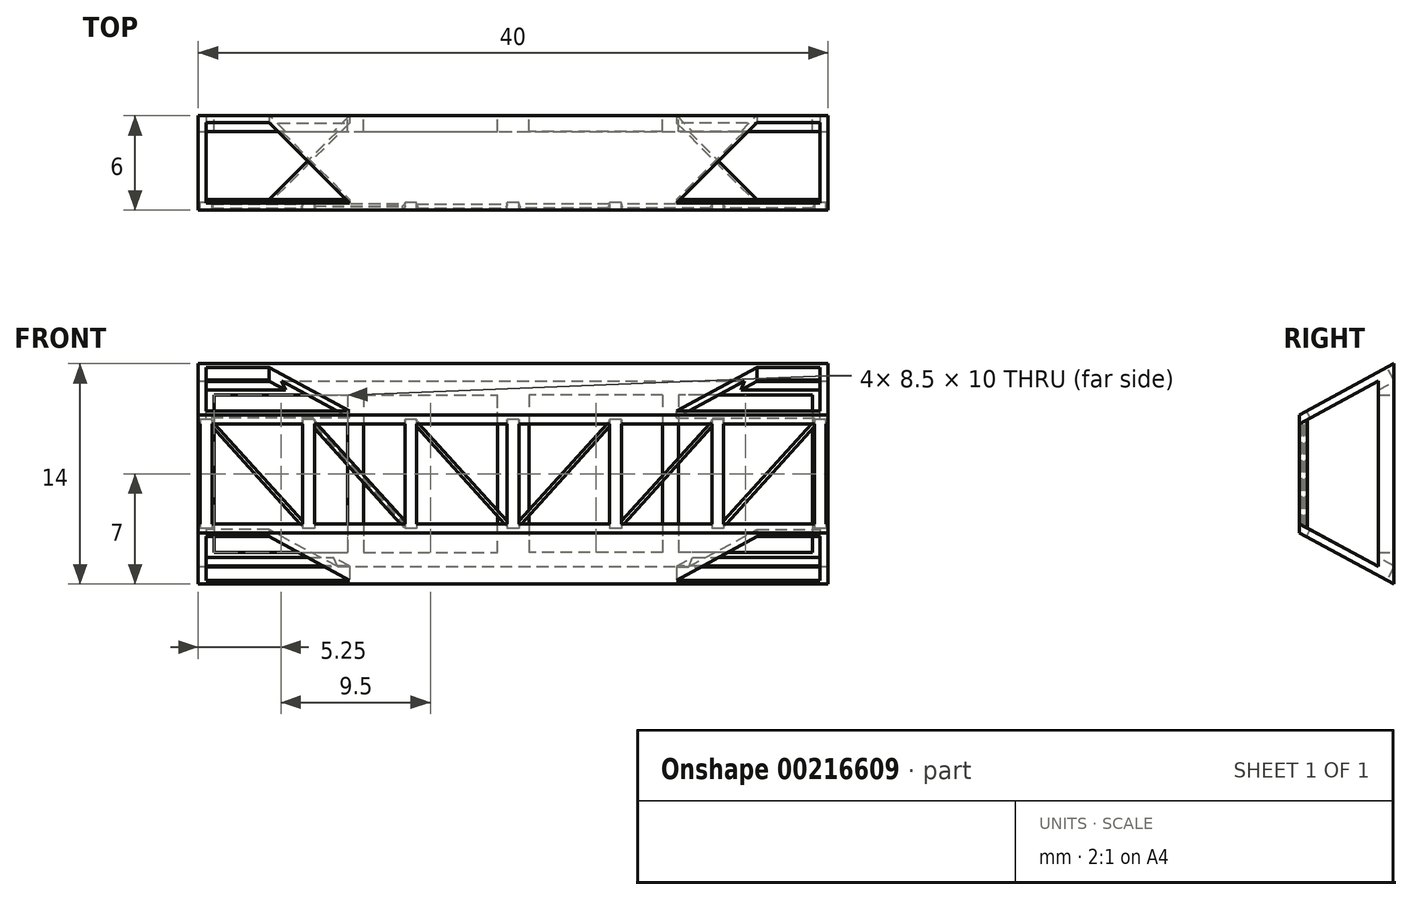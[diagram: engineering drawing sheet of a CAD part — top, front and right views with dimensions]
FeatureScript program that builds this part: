
annotation { "Feature Type Name" : "Feature", "Feature Type Description" : "" }
export const myFeature = defineFeature(function(context is Context, id is Id, definition is map)
    precondition{}
    {
        {
            var Q0;
            Q0=qCreatedBy(makeId("Right.planeOp"),FACE);
            var sketch = newSketch(context, id + "F0", { "sketchPlane" : qUnion([Q0])});
            skLineSegment(sketch, "E0", {"start": v(0, 0) * mm, "end": v(0, 7) * mm});
            skLineSegment(sketch, "E1", {"start": v(0, 0) * mm, "end": v(0, -7) * mm});
            skLineSegment(sketch, "E2", {"start": v(0, 0) * mm, "end": v(-6, 0) * mm});
            skLineSegment(sketch, "E3", {"start": v(-6, 0) * mm, "end": v(-6, 3.75) * mm});
            skLineSegment(sketch, "E4", {"start": v(-6, 3.75) * mm, "end": v(0, 7) * mm});
            skLineSegment(sketch, "E5.MirrorCS", {"start": v(-6, 0) * mm, "end": v(-6, -3.75) * mm});
            skLineSegment(sketch, "E6", {"start": v(-6, -3.75) * mm, "end": v(0, -7) * mm});
            skSolve(sketch);
        }
        {
            var Q0;
            Q0=makeQuery(id+"F0.imprint","IMPRINT",FACE,{"disambiguationData":[TD([[makeQuery(id+"F0.imprint","IMPRINT",EDGE,{"derivedFrom":sQuery(id+"F0.wireOp",EDGE,"E2")}),1.0]])]});
            var Q1;
            Q1=makeQuery(id+"F0.imprint","IMPRINT",FACE,{"disambiguationData":[TD([[makeQuery(id+"F0.imprint","IMPRINT",EDGE,{"derivedFrom":sQuery(id+"F0.wireOp",EDGE,"E0")}),1.0]])]});
            var Q2;
            Q2=sQuery(id+"F0.wireOp",EDGE,"E4");
            var Q3;
            Q3=sQuery(id+"F0.wireOp",EDGE,"E0");
            var Q4;
            Q4=sQuery(id+"F0.wireOp",EDGE,"E3");
            var Q5;
            Q5=sQuery(id+"F0.wireOp",EDGE,"E5.MirrorCS");
            var Q6;
            Q6=sQuery(id+"F0.wireOp",EDGE,"E1");
            var Q7;
            Q7=sQuery(id+"F0.wireOp",EDGE,"E6");
            extrude(context, id + "F1", {"entities" : qUnion([Q0, Q1]), "surfaceEntities" : qUnion([Q2, Q3, Q4, Q5, Q6, Q7]), "depth" : 20 * mm, "hasSecondDirection" : true, "secondDirectionOppositeDirection" : true, "secondDirectionDepth" : 20 * mm});
        }
        {
            var Q0;
            Q0=qCreatedBy(makeId("Right.planeOp"),FACE);
            var sketch = newSketch(context, id + "F2", { "sketchPlane" : qUnion([Q0])});
            skLineSegment(sketch, "E7", {"start": v(-2.76, 4.94) * mm, "end": v(-1, 5.9) * mm});
            skLineSegment(sketch, "E8", {"start": v(-2.76, 4.94) * mm, "end": v(-6, 3.19) * mm});
            skLineSegment(sketch, "E9", {"start": v(-1, 0) * mm, "end": v(-1, -5.89) * mm});
            skLineSegment(sketch, "E10", {"start": v(-1, 5.9) * mm, "end": v(-1, 0) * mm});
            skLineSegment(sketch, "E11", {"start": v(-6, -3.19) * mm, "end": v(-1, -5.89) * mm});
            skLineSegment(sketch, "E12", {"start": v(-6, 3.19) * mm, "end": v(-6, -3.19) * mm});
            skSolve(sketch);
        }
        {
            var Q0;
            Q0=makeQuery(id+"F2.imprint","IMPRINT",FACE,{"disambiguationData":[TD([[makeQuery(id+"F2.imprint","IMPRINT",EDGE,{"derivedFrom":sQuery(id+"F2.wireOp",EDGE,"E7")}),-1.0]])]});
            extrude(context, id + "F3", {"entities" : qUnion([Q0]), "operationType" : NewBodyOperationType.REMOVE, "oppositeDirection" : true, "depth" : 24 * mm, "hasSecondDirection" : true, "secondDirectionOppositeDirection" : false, "secondDirectionDepth" : 24 * mm});
        }
        {
            var Q0;
            Q0=makeQuery(id+"F1.opExtrude","SWEPT_FACE",FACE,{"disambiguationData":[OSD([sQuery(id+"F0.wireOp",EDGE,"E3"),sQuery(id+"F0.wireOp",EDGE,"E5.MirrorCS")])]});
            var sketch = newSketch(context, id + "F4", { "sketchPlane" : qUnion([Q0])});
            skLineSegment(sketch, "E13", {"start": v(0, 0) * mm, "end": v(0, 9.2) * mm, "construction": true});
            skPoint(sketch, "E13.endSnap0", {"position": v(0, 3.75) * mm});
            skLineSegment(sketch, "E14.bottom", {"start": v(0, 3.75) * mm, "end": v(-0.38, 3.75) * mm});
            skLineSegment(sketch, "E14.top", {"start": v(0, -3.75) * mm, "end": v(-0.37, -3.75) * mm});
            skLineSegment(sketch, "E14.left", {"start": v(0, 3.75) * mm, "end": v(0, -3.75) * mm});
            skLineSegment(sketch, "E14.right", {"start": v(-0.38, 3.75) * mm, "end": v(-0.37, -3.75) * mm});
            skLineSegment(sketch, "E15.bottom", {"start": v(0, 3.75) * mm, "end": v(0.38, 3.75) * mm});
            skLineSegment(sketch, "E15.top", {"start": v(0, -3.75) * mm, "end": v(0.38, -3.75) * mm});
            skLineSegment(sketch, "E15.right", {"start": v(0.38, 3.75) * mm, "end": v(0.38, -3.75) * mm});
            skLineSegment(sketch, "E16.trimOffspring", {"start": v(0, 0) * mm, "end": v(0, -10.66) * mm, "construction": true});
            skLineSegment(sketch, "E17.1.0.0", {"start": v(6.5, 3.75) * mm, "end": v(6.5, -3.75) * mm});
            skLineSegment(sketch, "E17.1.0.1", {"start": v(6.88, 3.75) * mm, "end": v(6.88, -3.75) * mm});
            skLineSegment(sketch, "E17.1.0.2", {"start": v(6.13, 3.75) * mm, "end": v(6.13, -3.75) * mm});
            skPoint(sketch, "E17.1.0.3", {"position": v(6.5, 3.75) * mm});
            skLineSegment(sketch, "E17.1.0.4", {"start": v(6.5, 3.75) * mm, "end": v(6.5, -3.75) * mm});
            skLineSegment(sketch, "E17.1.0.5", {"start": v(6.5, -3.75) * mm, "end": v(6.88, -3.75) * mm});
            skLineSegment(sketch, "E17.1.0.6", {"start": v(6.5, 3.75) * mm, "end": v(6.12, 3.75) * mm});
            skLineSegment(sketch, "E17.1.0.7", {"start": v(6.5, -3.75) * mm, "end": v(6.13, -3.75) * mm});
            skLineSegment(sketch, "E17.1.0.8", {"start": v(6.5, 3.75) * mm, "end": v(6.88, 3.75) * mm});
            skLineSegment(sketch, "E17.2.0.0", {"start": v(13, 3.75) * mm, "end": v(13, -3.75) * mm});
            skLineSegment(sketch, "E17.2.0.1", {"start": v(13.38, 3.75) * mm, "end": v(13.38, -3.75) * mm});
            skLineSegment(sketch, "E17.2.0.2", {"start": v(12.62, 3.75) * mm, "end": v(12.63, -3.75) * mm});
            skPoint(sketch, "E17.2.0.3", {"position": v(13, 3.75) * mm});
            skLineSegment(sketch, "E17.2.0.4", {"start": v(13, 3.75) * mm, "end": v(13, -3.75) * mm});
            skLineSegment(sketch, "E17.2.0.5", {"start": v(13, -3.75) * mm, "end": v(13.38, -3.75) * mm});
            skLineSegment(sketch, "E17.2.0.6", {"start": v(13, 3.75) * mm, "end": v(12.62, 3.75) * mm});
            skLineSegment(sketch, "E17.2.0.7", {"start": v(13, -3.75) * mm, "end": v(12.63, -3.75) * mm});
            skLineSegment(sketch, "E17.2.0.8", {"start": v(13, 3.75) * mm, "end": v(13.38, 3.75) * mm});
            skLineSegment(sketch, "E17.3.0.0", {"start": v(19.5, 3.75) * mm, "end": v(19.5, -3.75) * mm});
            skLineSegment(sketch, "E17.3.0.1", {"start": v(19.88, 3.75) * mm, "end": v(19.88, -3.75) * mm});
            skLineSegment(sketch, "E17.3.0.2", {"start": v(19.13, 3.75) * mm, "end": v(19.13, -3.75) * mm});
            skPoint(sketch, "E17.3.0.3", {"position": v(19.5, 3.75) * mm});
            skLineSegment(sketch, "E17.3.0.4", {"start": v(19.5, 3.75) * mm, "end": v(19.5, -3.75) * mm});
            skLineSegment(sketch, "E17.3.0.5", {"start": v(19.5, -3.75) * mm, "end": v(19.88, -3.75) * mm});
            skLineSegment(sketch, "E17.3.0.6", {"start": v(19.5, 3.75) * mm, "end": v(19.13, 3.75) * mm});
            skLineSegment(sketch, "E17.3.0.7", {"start": v(19.5, -3.75) * mm, "end": v(19.13, -3.75) * mm});
            skLineSegment(sketch, "E17.3.0.8", {"start": v(19.5, 3.75) * mm, "end": v(19.88, 3.75) * mm});
            skLineSegment(sketch, "E17.direction1", {"start": v(-0.37, -3.75) * mm, "end": v(6.13, -3.75) * mm, "construction": true});
            skLineSegment(sketch, "E18.1.0.0", {"start": v(-6.88, 3.75) * mm, "end": v(-6.87, -3.75) * mm});
            skLineSegment(sketch, "E18.1.0.1", {"start": v(-6.5, 3.75) * mm, "end": v(-6.5, -3.75) * mm});
            skLineSegment(sketch, "E18.1.0.2", {"start": v(-6.12, 3.75) * mm, "end": v(-6.12, -3.75) * mm});
            skPoint(sketch, "E18.1.0.3", {"position": v(-6.5, 3.75) * mm});
            skLineSegment(sketch, "E18.1.0.4", {"start": v(-6.5, 3.75) * mm, "end": v(-6.5, -3.75) * mm});
            skLineSegment(sketch, "E18.1.0.5", {"start": v(-6.5, 3.75) * mm, "end": v(-6.88, 3.75) * mm});
            skLineSegment(sketch, "E18.1.0.6", {"start": v(-6.5, 3.75) * mm, "end": v(-6.12, 3.75) * mm});
            skLineSegment(sketch, "E18.1.0.7", {"start": v(-6.5, -3.75) * mm, "end": v(-6.12, -3.75) * mm});
            skLineSegment(sketch, "E18.1.0.8", {"start": v(-6.5, -3.75) * mm, "end": v(-6.87, -3.75) * mm});
            skLineSegment(sketch, "E18.2.0.0", {"start": v(-13.38, 3.75) * mm, "end": v(-13.37, -3.75) * mm});
            skLineSegment(sketch, "E18.2.0.1", {"start": v(-13, 3.75) * mm, "end": v(-13, -3.75) * mm});
            skLineSegment(sketch, "E18.2.0.2", {"start": v(-12.62, 3.75) * mm, "end": v(-12.62, -3.75) * mm});
            skPoint(sketch, "E18.2.0.3", {"position": v(-13, 3.75) * mm});
            skLineSegment(sketch, "E18.2.0.4", {"start": v(-13, 3.75) * mm, "end": v(-13, -3.75) * mm});
            skLineSegment(sketch, "E18.2.0.5", {"start": v(-13, 3.75) * mm, "end": v(-13.38, 3.75) * mm});
            skLineSegment(sketch, "E18.2.0.6", {"start": v(-13, 3.75) * mm, "end": v(-12.62, 3.75) * mm});
            skLineSegment(sketch, "E18.2.0.7", {"start": v(-13, -3.75) * mm, "end": v(-12.62, -3.75) * mm});
            skLineSegment(sketch, "E18.2.0.8", {"start": v(-13, -3.75) * mm, "end": v(-13.37, -3.75) * mm});
            skLineSegment(sketch, "E18.3.0.0", {"start": v(-19.88, 3.75) * mm, "end": v(-19.88, -3.75) * mm});
            skLineSegment(sketch, "E18.3.0.1", {"start": v(-19.5, 3.75) * mm, "end": v(-19.5, -3.75) * mm});
            skLineSegment(sketch, "E18.3.0.2", {"start": v(-19.13, 3.75) * mm, "end": v(-19.13, -3.75) * mm});
            skPoint(sketch, "E18.3.0.3", {"position": v(-19.5, 3.75) * mm});
            skLineSegment(sketch, "E18.3.0.4", {"start": v(-19.5, 3.75) * mm, "end": v(-19.5, -3.75) * mm});
            skLineSegment(sketch, "E18.3.0.5", {"start": v(-19.5, 3.75) * mm, "end": v(-19.88, 3.75) * mm});
            skLineSegment(sketch, "E18.3.0.6", {"start": v(-19.5, 3.75) * mm, "end": v(-19.13, 3.75) * mm});
            skLineSegment(sketch, "E18.3.0.7", {"start": v(-19.5, -3.75) * mm, "end": v(-19.13, -3.75) * mm});
            skLineSegment(sketch, "E18.3.0.8", {"start": v(-19.5, -3.75) * mm, "end": v(-19.88, -3.75) * mm});
            skLineSegment(sketch, "E18.direction1", {"start": v(-0.37, -3.75) * mm, "end": v(-6.87, -3.75) * mm, "construction": true});
            skSolve(sketch);
        }
        {
            var Q0;
            Q0=qSketchRegion(id+"F4",true);
            extrude(context, id + "F5", {"entities" : qUnion([Q0]), "operationType" : NewBodyOperationType.ADD, "oppositeDirection" : true, "depth" : .5 * mm});
        }
        {
            var Q0;
            Q0=qCreatedBy(makeId("Front.planeOp"),FACE);
            cPlane(context, id + "F6", {"entities" : qUnion([Q0]), "cplaneType" : CPlaneType.OFFSET, "offset" : 5.75 * mm, "width" : 150 * mm, "height" : 150 * mm});
        }
        {
            var Q0;
            Q0=qCreatedBy(id+"F6.planeOp",FACE);
            var sketch = newSketch(context, id + "F7", { "sketchPlane" : qUnion([Q0])});
            skLineSegment(sketch, "E19", {"start": v(-0.38, -3.18) * mm, "end": v(-0.18, -3.4) * mm});
            skLineSegment(sketch, "E20", {"start": v(-0.18, -3.4) * mm, "end": v(-0.09, -3.32) * mm});
            skLineSegment(sketch, "E21", {"start": v(-0.18, -3.4) * mm, "end": v(-0.27, -3.48) * mm});
            skLineSegment(sketch, "E22", {"start": v(-6.18, 3.43) * mm, "end": v(-0.09, -3.32) * mm});
            skLineSegment(sketch, "E23.MirrorCS", {"start": v(0.18, -3.4) * mm, "end": v(0.09, -3.32) * mm});
            skLineSegment(sketch, "E24.MirrorCS", {"start": v(0.18, -3.4) * mm, "end": v(0.27, -3.48) * mm});
            skLineSegment(sketch, "E25.MirrorCS", {"start": v(6.37, 3.27) * mm, "end": v(6.18, 3.43) * mm});
            skLineSegment(sketch, "E26.MirrorCS", {"start": v(0.38, -3.18) * mm, "end": v(0.18, -3.4) * mm});
            skLineSegment(sketch, "E27.MirrorCS", {"start": v(6.18, 3.43) * mm, "end": v(0.09, -3.32) * mm});
            skLineSegment(sketch, "E28.1.0.1", {"start": v(-12.68, 3.43) * mm, "end": v(-6.59, -3.32) * mm});
            skLineSegment(sketch, "E28.1.0.2", {"start": v(-12.87, 3.27) * mm, "end": v(-12.68, 3.43) * mm});
            skLineSegment(sketch, "E28.1.0.3", {"start": v(-6.88, -3.18) * mm, "end": v(-6.68, -3.4) * mm});
            skLineSegment(sketch, "E28.1.0.5", {"start": v(-6.68, -3.4) * mm, "end": v(-6.59, -3.32) * mm});
            skLineSegment(sketch, "E28.2.0.1", {"start": v(-19.18, 3.43) * mm, "end": v(-13.09, -3.32) * mm});
            skLineSegment(sketch, "E28.2.0.3", {"start": v(-13.38, -3.18) * mm, "end": v(-13.18, -3.4) * mm});
            skLineSegment(sketch, "E28.2.0.4", {"start": v(-13.18, -3.4) * mm, "end": v(-13.27, -3.48) * mm});
            skLineSegment(sketch, "E28.2.0.5", {"start": v(-13.18, -3.4) * mm, "end": v(-13.09, -3.32) * mm});
            skLineSegment(sketch, "E28.direction1", {"start": v(-0.27, -3.48) * mm, "end": v(-6.77, -3.48) * mm, "construction": true});
            skLineSegment(sketch, "E29.1.0.1", {"start": v(12.68, 3.43) * mm, "end": v(6.59, -3.32) * mm});
            skLineSegment(sketch, "E29.1.0.2", {"start": v(12.87, 3.27) * mm, "end": v(12.68, 3.43) * mm});
            skLineSegment(sketch, "E29.1.0.3", {"start": v(6.88, -3.18) * mm, "end": v(6.68, -3.4) * mm});
            skLineSegment(sketch, "E29.1.0.4", {"start": v(6.68, -3.4) * mm, "end": v(6.77, -3.48) * mm});
            skLineSegment(sketch, "E29.1.0.5", {"start": v(6.68, -3.4) * mm, "end": v(6.59, -3.32) * mm});
            skLineSegment(sketch, "E29.2.0.1", {"start": v(19.18, 3.43) * mm, "end": v(13.09, -3.32) * mm});
            skLineSegment(sketch, "E29.2.0.2", {"start": v(19.37, 3.27) * mm, "end": v(19.18, 3.43) * mm});
            skLineSegment(sketch, "E29.2.0.3", {"start": v(13.38, -3.18) * mm, "end": v(13.18, -3.4) * mm});
            skLineSegment(sketch, "E29.2.0.4", {"start": v(13.18, -3.4) * mm, "end": v(13.27, -3.48) * mm});
            skLineSegment(sketch, "E29.2.0.5", {"start": v(13.18, -3.4) * mm, "end": v(13.09, -3.32) * mm});
            skLineSegment(sketch, "E29.direction1", {"start": v(0.09, -3.32) * mm, "end": v(6.59, -3.32) * mm, "construction": true});
            skLineSegment(sketch, "E30.MirrorCS", {"start": v(19.67, -3.5) * mm, "end": v(19.78, -3.57) * mm});
            skLineSegment(sketch, "E31", {"start": v(-13.38, -3.18) * mm, "end": v(-19.28, 3.35) * mm});
            skLineSegment(sketch, "E32", {"start": v(-19.18, 3.43) * mm, "end": v(-19.28, 3.35) * mm});
            skLineSegment(sketch, "E33", {"start": v(-6.88, -3.18) * mm, "end": v(-12.75, 3.27) * mm});
            skLineSegment(sketch, "E34", {"start": v(-12.75, 3.27) * mm, "end": v(-12.8, 3.33) * mm});
            skLineSegment(sketch, "E35", {"start": v(-0.38, -3.18) * mm, "end": v(-6.28, 3.35) * mm});
            skLineSegment(sketch, "E36", {"start": v(-6.18, 3.43) * mm, "end": v(-6.28, 3.35) * mm});
            skLineSegment(sketch, "E37", {"start": v(0.38, -3.18) * mm, "end": v(6.28, 3.35) * mm});
            skLineSegment(sketch, "E38", {"start": v(6.88, -3.18) * mm, "end": v(12.78, 3.35) * mm});
            skLineSegment(sketch, "E39", {"start": v(13.38, -3.18) * mm, "end": v(19.28, 3.35) * mm});
            skSolve(sketch);
        }
        {
            var Q0;
            Q0=makeQuery(id+"F7.imprint","IMPRINT",FACE,{"disambiguationData":[TD([[makeQuery(id+"F7.imprint","IMPRINT",EDGE,{"derivedFrom":sQuery(id+"F7.wireOp",EDGE,"E28.2.0.1")}),-1.0]])]});
            var Q1;
            Q1=sQuery(id+"F7.wireOp",EDGE,"E31");
            revolve(context, id + "F8", {"operationType" : NewBodyOperationType.ADD, "entities" : qUnion([Q0]), "axis" : qUnion([Q1]), "revolveType" : RevolveType.FULL});
        }
        {
            var Q0;
            {var subQ1=sQuery(id+"F7.wireOp",EDGE,"E28.1.0.1");Q0=makeQuery(id+"F7.imprint","IMPRINT",FACE,{"disambiguationData":[TD([[makeQuery(id+"F7.imprint","IMPRINT",EDGE,{"derivedFrom":subQ1}),-1.0]])]});}
            var Q1;
            Q1=sQuery(id+"F7.wireOp",EDGE,"E34");
            revolve(context, id + "F9", {"operationType" : NewBodyOperationType.ADD, "entities" : qUnion([Q0]), "axis" : qUnion([Q1]), "revolveType" : RevolveType.FULL});
        }
        {
            var Q0;
            Q0=makeQuery(id+"F7.imprint","IMPRINT",FACE,{"disambiguationData":[TD([[makeQuery(id+"F7.imprint","IMPRINT",EDGE,{"derivedFrom":sQuery(id+"F7.wireOp",EDGE,"E19")}),1.0]])]});
            var Q1;
            Q1=sQuery(id+"F7.wireOp",EDGE,"E35");
            revolve(context, id + "F10", {"operationType" : NewBodyOperationType.ADD, "entities" : qUnion([Q0]), "axis" : qUnion([Q1]), "revolveType" : RevolveType.FULL});
        }
        {
            var Q0;
            Q0=makeQuery(id+"F7.imprint","IMPRINT",FACE,{"disambiguationData":[TD([[makeQuery(id+"F7.imprint","IMPRINT",EDGE,{"derivedFrom":sQuery(id+"F7.wireOp",EDGE,"E23.MirrorCS")}),-1.0]])]});
            var Q1;
            Q1=sQuery(id+"F7.wireOp",EDGE,"E37");
            revolve(context, id + "F11", {"operationType" : NewBodyOperationType.ADD, "entities" : qUnion([Q0]), "axis" : qUnion([Q1]), "revolveType" : RevolveType.FULL});
        }
        {
            var Q0;
            {var subQ1=sQuery(id+"F7.wireOp",EDGE,"E29.1.0.1");Q0=makeQuery(id+"F7.imprint","IMPRINT",FACE,{"disambiguationData":[TD([[makeQuery(id+"F7.imprint","IMPRINT",EDGE,{"derivedFrom":subQ1}),1.0]])]});}
            var Q1;
            Q1=sQuery(id+"F7.wireOp",EDGE,"E38");
            revolve(context, id + "F12", {"operationType" : NewBodyOperationType.ADD, "entities" : qUnion([Q0]), "axis" : qUnion([Q1]), "revolveType" : RevolveType.FULL});
        }
        {
            var Q0;
            {var subQ1=sQuery(id+"F7.wireOp",EDGE,"E29.2.0.1");Q0=makeQuery(id+"F7.imprint","IMPRINT",FACE,{"disambiguationData":[TD([[makeQuery(id+"F7.imprint","IMPRINT",EDGE,{"derivedFrom":subQ1}),1.0]])]});}
            var Q1;
            Q1=sQuery(id+"F7.wireOp",EDGE,"E39");
            revolve(context, id + "F13", {"operationType" : NewBodyOperationType.ADD, "entities" : qUnion([Q0]), "axis" : qUnion([Q1]), "revolveType" : RevolveType.FULL});
        }
        {
            var Q0;
            Q0=makeQuery(id+"F1.opExtrude","SWEPT_FACE",FACE,{"disambiguationData":[OSD([sQuery(id+"F0.wireOp",EDGE,"E4")])]});
            var sketch = newSketch(context, id + "F14", { "sketchPlane" : qUnion([Q0])});
            skLineSegment(sketch, "E40", {"start": v(0, 3.33) * mm, "end": v(20, 3.33) * mm});
            skLineSegment(sketch, "E41", {"start": v(20, 3.33) * mm, "end": v(20, -3.49) * mm});
            skLineSegment(sketch, "E42", {"start": v(0, 3.33) * mm, "end": v(0, 2.83) * mm});
            skLineSegment(sketch, "E43", {"start": v(0, 2.83) * mm, "end": v(20, 2.83) * mm});
            skLineSegment(sketch, "E44", {"start": v(20, 2.83) * mm, "end": v(19.5, 2.83) * mm});
            skLineSegment(sketch, "E45", {"start": v(19.5, 2.83) * mm, "end": v(19.5, -3.49) * mm});
            skLineSegment(sketch, "E46", {"start": v(19.5, -3.49) * mm, "end": v(19.5, -2.99) * mm});
            skLineSegment(sketch, "E47", {"start": v(19.5, -2.99) * mm, "end": v(0, -2.99) * mm});
            skLineSegment(sketch, "E48", {"start": v(0, 2.83) * mm, "end": v(4, 2.83) * mm});
            skLineSegment(sketch, "E49", {"start": v(4, 2.83) * mm, "end": v(4.75, 2.83) * mm});
            skLineSegment(sketch, "E50", {"start": v(4.75, 2.83) * mm, "end": v(14.75, 2.83) * mm});
            skLineSegment(sketch, "E51", {"start": v(19.5, 2.83) * mm, "end": v(15.5, 2.83) * mm});
            skLineSegment(sketch, "E52", {"start": v(0, -2.99) * mm, "end": v(10, -2.99) * mm});
            skLineSegment(sketch, "E53", {"start": v(10, -2.99) * mm, "end": v(9.62, -2.99) * mm});
            skLineSegment(sketch, "E54", {"start": v(9.62, -2.99) * mm, "end": v(4, 2.83) * mm});
            skLineSegment(sketch, "E55", {"start": v(10, -2.99) * mm, "end": v(10.38, -2.99) * mm});
            skLineSegment(sketch, "E56", {"start": v(10.38, -2.99) * mm, "end": v(15.5, 2.83) * mm});
            skLineSegment(sketch, "E57", {"start": v(10, -2.99) * mm, "end": v(10, -2.6) * mm});
            skLineSegment(sketch, "E58", {"start": v(4.75, 2.83) * mm, "end": v(10, -2.6) * mm});
            skPoint(sketch, "E59.orphan", {"position": v(10, -2.49) * mm});
            skLineSegment(sketch, "E60", {"start": v(10, -2.6) * mm, "end": v(14.75, 2.83) * mm});
            skLineSegment(sketch, "E61.MirrorCS", {"start": v(-20, 3.33) * mm, "end": v(-20, -3.49) * mm});
            skLineSegment(sketch, "E62.MirrorCS", {"start": v(0, 2.83) * mm, "end": v(-20, 2.83) * mm});
            skLineSegment(sketch, "E63.MirrorCS", {"start": v(-4.75, 2.83) * mm, "end": v(-14.75, 2.83) * mm});
            skLineSegment(sketch, "E64.MirrorCS", {"start": v(0, 3.33) * mm, "end": v(-20, 3.33) * mm});
            skLineSegment(sketch, "E65.MirrorCS", {"start": v(0, 3.33) * mm, "end": v(0, -3.49) * mm});
            skLineSegment(sketch, "E66.MirrorCS", {"start": v(0, 2.83) * mm, "end": v(-4, 2.83) * mm});
            skLineSegment(sketch, "E67.MirrorCS", {"start": v(-10.38, -2.99) * mm, "end": v(-15.5, 2.83) * mm});
            skLineSegment(sketch, "E68.MirrorCS", {"start": v(-19.5, 2.83) * mm, "end": v(-19.5, -3.49) * mm});
            skLineSegment(sketch, "E69.MirrorCS", {"start": v(-20, -3.49) * mm, "end": v(0, -3.49) * mm});
            skLineSegment(sketch, "E70.MirrorCS", {"start": v(-10, -2.6) * mm, "end": v(-14.75, 2.83) * mm});
            skLineSegment(sketch, "E71.MirrorCS", {"start": v(-4.75, 2.83) * mm, "end": v(-10, -2.6) * mm});
            skPoint(sketch, "E72.MirrorP", {"position": v(-10, -2.49) * mm});
            skLineSegment(sketch, "E73.MirrorCS", {"start": v(-19.5, -2.99) * mm, "end": v(0, -2.99) * mm});
            skLineSegment(sketch, "E74.MirrorCS", {"start": v(-9.62, -2.99) * mm, "end": v(-4, 2.83) * mm});
            skLineSegment(sketch, "E75.MirrorCS", {"start": v(-10, -2.99) * mm, "end": v(-10, -2.6) * mm});
            skLineSegment(sketch, "E76.MirrorCS", {"start": v(-10, -2.99) * mm, "end": v(-10.38, -2.99) * mm});
            skLineSegment(sketch, "E77.MirrorCS", {"start": v(-10, -2.99) * mm, "end": v(-9.62, -2.99) * mm});
            skLineSegment(sketch, "E78.MirrorCS", {"start": v(-19.5, -3.49) * mm, "end": v(-19.5, -2.99) * mm});
            skLineSegment(sketch, "E79.MirrorCS", {"start": v(-4, 2.83) * mm, "end": v(-4.75, 2.83) * mm});
            skLineSegment(sketch, "E80.MirrorCS", {"start": v(-20, 2.83) * mm, "end": v(-19.5, 2.83) * mm});
            skLineSegment(sketch, "E81.MirrorCS", {"start": v(0, -2.99) * mm, "end": v(-10, -2.99) * mm});
            skLineSegment(sketch, "E82.MirrorCS", {"start": v(-19.5, 2.83) * mm, "end": v(-15.5, 2.83) * mm});
            skSolve(sketch);
        }
        {
            var Q0;
            Q0=makeQuery(id+"F1.opExtrude","SWEPT_FACE",FACE,{"disambiguationData":[OSD([sQuery(id+"F0.wireOp",EDGE,"E6")])]});
            var sketch = newSketch(context, id + "F15", { "sketchPlane" : qUnion([Q0])});
            skLineSegment(sketch, "E83", {"start": v(0, 3.5) * mm, "end": v(20, 3.5) * mm});
            skLineSegment(sketch, "E84", {"start": v(20, 3.5) * mm, "end": v(20, -7.07) * mm});
            skLineSegment(sketch, "E85", {"start": v(0, 3.5) * mm, "end": v(0, 3) * mm});
            skLineSegment(sketch, "E86", {"start": v(0, 3) * mm, "end": v(20, 3) * mm});
            skLineSegment(sketch, "E87", {"start": v(20, 3) * mm, "end": v(19.5, 3) * mm});
            skLineSegment(sketch, "E88", {"start": v(19.5, 3) * mm, "end": v(19.5, -3.32) * mm});
            skLineSegment(sketch, "E89", {"start": v(19.5, -3.32) * mm, "end": v(19.5, -2.82) * mm});
            skLineSegment(sketch, "E90", {"start": v(19.5, -2.82) * mm, "end": v(0, -2.82) * mm});
            skLineSegment(sketch, "E91", {"start": v(0, 3) * mm, "end": v(4, 3) * mm});
            skLineSegment(sketch, "E92", {"start": v(4, 3) * mm, "end": v(4.75, 3) * mm});
            skLineSegment(sketch, "E93", {"start": v(4.75, 3) * mm, "end": v(14.75, 3) * mm});
            skLineSegment(sketch, "E94", {"start": v(19.5, 3) * mm, "end": v(15.5, 3) * mm});
            skLineSegment(sketch, "E95", {"start": v(0, -2.82) * mm, "end": v(10, -2.82) * mm});
            skLineSegment(sketch, "E96", {"start": v(10, -2.82) * mm, "end": v(9.62, -2.82) * mm});
            skLineSegment(sketch, "E97", {"start": v(9.62, -2.82) * mm, "end": v(4, 3) * mm});
            skLineSegment(sketch, "E98", {"start": v(10, -2.82) * mm, "end": v(10.37, -2.82) * mm});
            skLineSegment(sketch, "E99", {"start": v(10.37, -2.82) * mm, "end": v(15.5, 3) * mm});
            skLineSegment(sketch, "E100", {"start": v(10, -2.82) * mm, "end": v(10, -2.43) * mm});
            skLineSegment(sketch, "E101", {"start": v(4.75, 3) * mm, "end": v(10, -2.43) * mm});
            skPoint(sketch, "E102.orphan", {"position": v(10, -2.32) * mm});
            skLineSegment(sketch, "E103", {"start": v(10, -2.43) * mm, "end": v(14.75, 3) * mm});
            skLineSegment(sketch, "E104.MirrorCS", {"start": v(-20, 3.5) * mm, "end": v(-20, -3.32) * mm});
            skLineSegment(sketch, "E105.MirrorCS", {"start": v(0, 3) * mm, "end": v(-19.57, 3) * mm});
            skLineSegment(sketch, "E106.MirrorCS", {"start": v(-4.75, 3) * mm, "end": v(-14.75, 3) * mm});
            skLineSegment(sketch, "E107.MirrorCS", {"start": v(0, 3.5) * mm, "end": v(-20, 3.5) * mm});
            skLineSegment(sketch, "E108.MirrorCS", {"start": v(0, 3.5) * mm, "end": v(0, -3.32) * mm});
            skLineSegment(sketch, "E109.MirrorCS", {"start": v(0, 3) * mm, "end": v(-4, 3) * mm});
            skLineSegment(sketch, "E110.MirrorCS", {"start": v(-10.38, -2.82) * mm, "end": v(-15.5, 3) * mm});
            skLineSegment(sketch, "E111.MirrorCS", {"start": v(-19.5, 3) * mm, "end": v(-19.5, -7.07) * mm});
            skLineSegment(sketch, "E112.MirrorCS", {"start": v(-20, -3.32) * mm, "end": v(0, -3.32) * mm});
            skLineSegment(sketch, "E113.MirrorCS", {"start": v(-10, -2.43) * mm, "end": v(-14.75, 3) * mm});
            skLineSegment(sketch, "E114.MirrorCS", {"start": v(-4.75, 3) * mm, "end": v(-10, -2.43) * mm});
            skPoint(sketch, "E115.MirrorP", {"position": v(-10, -2.32) * mm});
            skLineSegment(sketch, "E116.MirrorCS", {"start": v(-19.5, -2.82) * mm, "end": v(0.43, -2.82) * mm});
            skLineSegment(sketch, "E117.MirrorCS", {"start": v(-9.63, -2.82) * mm, "end": v(-4, 3) * mm});
            skLineSegment(sketch, "E118.MirrorCS", {"start": v(-10, -2.82) * mm, "end": v(-10, -2.43) * mm});
            skLineSegment(sketch, "E119.MirrorCS", {"start": v(-10, -2.82) * mm, "end": v(-10.38, -2.82) * mm});
            skLineSegment(sketch, "E120.MirrorCS", {"start": v(-10, -2.82) * mm, "end": v(-9.63, -2.82) * mm});
            skLineSegment(sketch, "E121.MirrorCS", {"start": v(-19.5, -7.07) * mm, "end": v(-19.5, -2.82) * mm});
            skLineSegment(sketch, "E122.MirrorCS", {"start": v(-4, 3) * mm, "end": v(-4.75, 3) * mm});
            skLineSegment(sketch, "E123.MirrorCS", {"start": v(-19.57, 3) * mm, "end": v(-19.5, 3) * mm});
            skLineSegment(sketch, "E124.MirrorCS", {"start": v(0.43, -2.82) * mm, "end": v(-10, -2.82) * mm});
            skLineSegment(sketch, "E125.MirrorCS", {"start": v(-19.5, 3) * mm, "end": v(-15.5, 3) * mm});
            skSolve(sketch);
        }
        {
            var Q0;
            Q0=makeQuery(id+"F1.opExtrude","SWEPT_FACE",FACE,{"disambiguationData":[OSD([sQuery(id+"F0.wireOp",EDGE,"E0"),sQuery(id+"F0.wireOp",EDGE,"E1")])]});
            var sketch = newSketch(context, id + "F16", { "sketchPlane" : qUnion([Q0])});
            skLineSegment(sketch, "E126", {"start": v(0, 0) * mm, "end": v(0, 10.47) * mm});
            skLineSegment(sketch, "E127", {"start": v(0, 10.47) * mm, "end": v(0, -11.27) * mm});
            skLineSegment(sketch, "E128", {"start": v(-1, 0) * mm, "end": v(-1, 5) * mm});
            skLineSegment(sketch, "E129", {"start": v(-19, 5) * mm, "end": v(-19, -5) * mm});
            skLineSegment(sketch, "E130", {"start": v(-20, -7) * mm, "end": v(-20, -5) * mm});
            skLineSegment(sketch, "E131", {"start": v(-19, -5) * mm, "end": v(-10.5, -5) * mm});
            skLineSegment(sketch, "E132", {"start": v(-1, 0) * mm, "end": v(-1, -5) * mm});
            skLineSegment(sketch, "E133", {"start": v(-19, 5) * mm, "end": v(-10.5, 5) * mm});
            skLineSegment(sketch, "E134", {"start": v(-10.5, 5) * mm, "end": v(-10.5, -5) * mm});
            skLineSegment(sketch, "E135", {"start": v(-9.5, 5) * mm, "end": v(-9.5, -5) * mm});
            skLineSegment(sketch, "E136.trimOffspring", {"start": v(-9.5, 5) * mm, "end": v(-1, 5) * mm});
            skPoint(sketch, "E137.orphan", {"position": v(-10, 5) * mm});
            skPoint(sketch, "E138.end.orphan", {"position": v(0, 5) * mm});
            skPoint(sketch, "E138.start.orphan", {"position": v(0, 7) * mm});
            skLineSegment(sketch, "E139.trimOffspring", {"start": v(-9.5, -5) * mm, "end": v(-1, -5) * mm});
            skPoint(sketch, "E140.trimOffspring.end.orphan", {"position": v(-20, 5) * mm});
            skPoint(sketch, "E141.orphan", {"position": v(0, -5) * mm});
            skLineSegment(sketch, "E142.MirrorCS", {"start": v(9.5, 5) * mm, "end": v(1, 5) * mm});
            skLineSegment(sketch, "E143.MirrorCS", {"start": v(19, -5) * mm, "end": v(10.5, -5) * mm});
            skLineSegment(sketch, "E144.MirrorCS", {"start": v(9.5, -5) * mm, "end": v(1, -5) * mm});
            skLineSegment(sketch, "E145.MirrorCS", {"start": v(1, 0) * mm, "end": v(1, 5) * mm});
            skLineSegment(sketch, "E146.MirrorCS", {"start": v(1, 0) * mm, "end": v(1, -5) * mm});
            skPoint(sketch, "E147.MirrorP", {"position": v(20, 5) * mm});
            skLineSegment(sketch, "E148.MirrorCS", {"start": v(9.5, 5) * mm, "end": v(9.5, -5) * mm});
            skLineSegment(sketch, "E149.MirrorCS", {"start": v(19, 5) * mm, "end": v(19, -5) * mm});
            skLineSegment(sketch, "E150.MirrorCS", {"start": v(20, -7) * mm, "end": v(20, -5) * mm});
            skLineSegment(sketch, "E151.MirrorCS", {"start": v(19, 5) * mm, "end": v(10.5, 5) * mm});
            skLineSegment(sketch, "E152.MirrorCS", {"start": v(10.5, 5) * mm, "end": v(10.5, -5) * mm});
            skPoint(sketch, "E153.MirrorP", {"position": v(10, 5) * mm});
            skSolve(sketch);
        }
        {
            var Q0;
            Q0=makeQuery(id+"F16.imprint","IMPRINT",FACE,{"disambiguationData":[TD([[makeQuery(id+"F16.imprint","IMPRINT",EDGE,{"derivedFrom":sQuery(id+"F16.wireOp",EDGE,"E129")}),1.0]])]});
            var Q1;
            Q1=makeQuery(id+"F16.imprint","IMPRINT",FACE,{"disambiguationData":[TD([[makeQuery(id+"F16.imprint","IMPRINT",EDGE,{"derivedFrom":sQuery(id+"F16.wireOp",EDGE,"E128")}),1.0]])]});
            var Q2;
            Q2=makeQuery(id+"F16.imprint","IMPRINT",FACE,{"disambiguationData":[TD([[makeQuery(id+"F16.imprint","IMPRINT",EDGE,{"derivedFrom":sQuery(id+"F16.wireOp",EDGE,"E142.MirrorCS")}),1.0]])]});
            var Q3;
            Q3=makeQuery(id+"F16.imprint","IMPRINT",FACE,{"disambiguationData":[TD([[makeQuery(id+"F16.imprint","IMPRINT",EDGE,{"derivedFrom":sQuery(id+"F16.wireOp",EDGE,"E143.MirrorCS")}),-1.0]])]});
            extrude(context, id + "F17", {"entities" : qUnion([Q0, Q1, Q2, Q3]), "operationType" : NewBodyOperationType.REMOVE, "oppositeDirection" : true, "depth" : 1 * mm});
        }
        {
            var Q0;
            Q0=makeQuery(id+"F14.imprint","IMPRINT",FACE,{"disambiguationData":[TD([[makeQuery(id+"F14.imprint","IMPRINT",EDGE,{"derivedFrom":sQuery(id+"F14.wireOp",EDGE,"E67.MirrorCS")}),1.0]])]});
            var Q1;
            Q1=makeQuery(id+"F14.imprint","IMPRINT",FACE,{"disambiguationData":[TD([[makeQuery(id+"F14.imprint","IMPRINT",EDGE,{"derivedFrom":sQuery(id+"F14.wireOp",EDGE,"E63.MirrorCS")}),1.0]])]});
            var Q2;
            {var subQ0=sQuery(id+"F14.wireOp",EDGE,"E66.MirrorCS");Q2=makeQuery(id+"F14.imprint","IMPRINT",FACE,{"disambiguationData":[TD([[makeQuery(id+"F14.imprint","IMPRINT",EDGE,{"derivedFrom":subQ0}),1.0]])]});}
            var Q3;
            {var subQ0=sQuery(id+"F14.wireOp",EDGE,"E48");Q3=makeQuery(id+"F14.imprint","IMPRINT",FACE,{"disambiguationData":[TD([[makeQuery(id+"F14.imprint","IMPRINT",EDGE,{"derivedFrom":subQ0}),-1.0]])]});}
            var Q4;
            Q4=makeQuery(id+"F14.imprint","IMPRINT",FACE,{"disambiguationData":[TD([[makeQuery(id+"F14.imprint","IMPRINT",EDGE,{"derivedFrom":sQuery(id+"F14.wireOp",EDGE,"E50")}),-1.0]])]});
            var Q5;
            Q5=makeQuery(id+"F14.imprint","IMPRINT",FACE,{"disambiguationData":[TD([[makeQuery(id+"F14.imprint","IMPRINT",EDGE,{"derivedFrom":sQuery(id+"F14.wireOp",EDGE,"E45")}),-1.0]])]});
            extrude(context, id + "F18", {"entities" : qUnion([Q0, Q1, Q2, Q3, Q4, Q5]), "operationType" : NewBodyOperationType.REMOVE, "oppositeDirection" : true, "depth" : 1 * mm});
        }
        {
            var Q0;
            Q0=makeQuery(id+"F15.imprint","IMPRINT",FACE,{"disambiguationData":[TD([[makeQuery(id+"F15.imprint","IMPRINT",EDGE,{"derivedFrom":sQuery(id+"F15.wireOp",EDGE,"E110.MirrorCS")}),1.0]])]});
            var Q1;
            Q1=makeQuery(id+"F15.imprint","IMPRINT",FACE,{"disambiguationData":[TD([[makeQuery(id+"F15.imprint","IMPRINT",EDGE,{"derivedFrom":sQuery(id+"F15.wireOp",EDGE,"E106.MirrorCS")}),1.0]])]});
            var Q2;
            {var subQ0=sQuery(id+"F15.wireOp",EDGE,"E109.MirrorCS");Q2=makeQuery(id+"F15.imprint","IMPRINT",FACE,{"disambiguationData":[TD([[makeQuery(id+"F15.imprint","IMPRINT",EDGE,{"derivedFrom":subQ0}),1.0]])]});}
            var Q3;
            {var subQ1=sQuery(id+"F15.wireOp",EDGE,"E91");Q3=makeQuery(id+"F15.imprint","IMPRINT",FACE,{"disambiguationData":[TD([[makeQuery(id+"F15.imprint","IMPRINT",EDGE,{"derivedFrom":subQ1}),-1.0]])]});}
            var Q4;
            Q4=makeQuery(id+"F15.imprint","IMPRINT",FACE,{"disambiguationData":[TD([[makeQuery(id+"F15.imprint","IMPRINT",EDGE,{"derivedFrom":sQuery(id+"F15.wireOp",EDGE,"E93")}),-1.0]])]});
            var Q5;
            Q5=makeQuery(id+"F15.imprint","IMPRINT",FACE,{"disambiguationData":[TD([[makeQuery(id+"F15.imprint","IMPRINT",EDGE,{"derivedFrom":sQuery(id+"F15.wireOp",EDGE,"E88")}),-1.0]])]});
            extrude(context, id + "F19", {"entities" : qUnion([Q0, Q1, Q2, Q3, Q4, Q5]), "operationType" : NewBodyOperationType.REMOVE, "oppositeDirection" : true, "depth" : 1 * mm});
        }
    });
